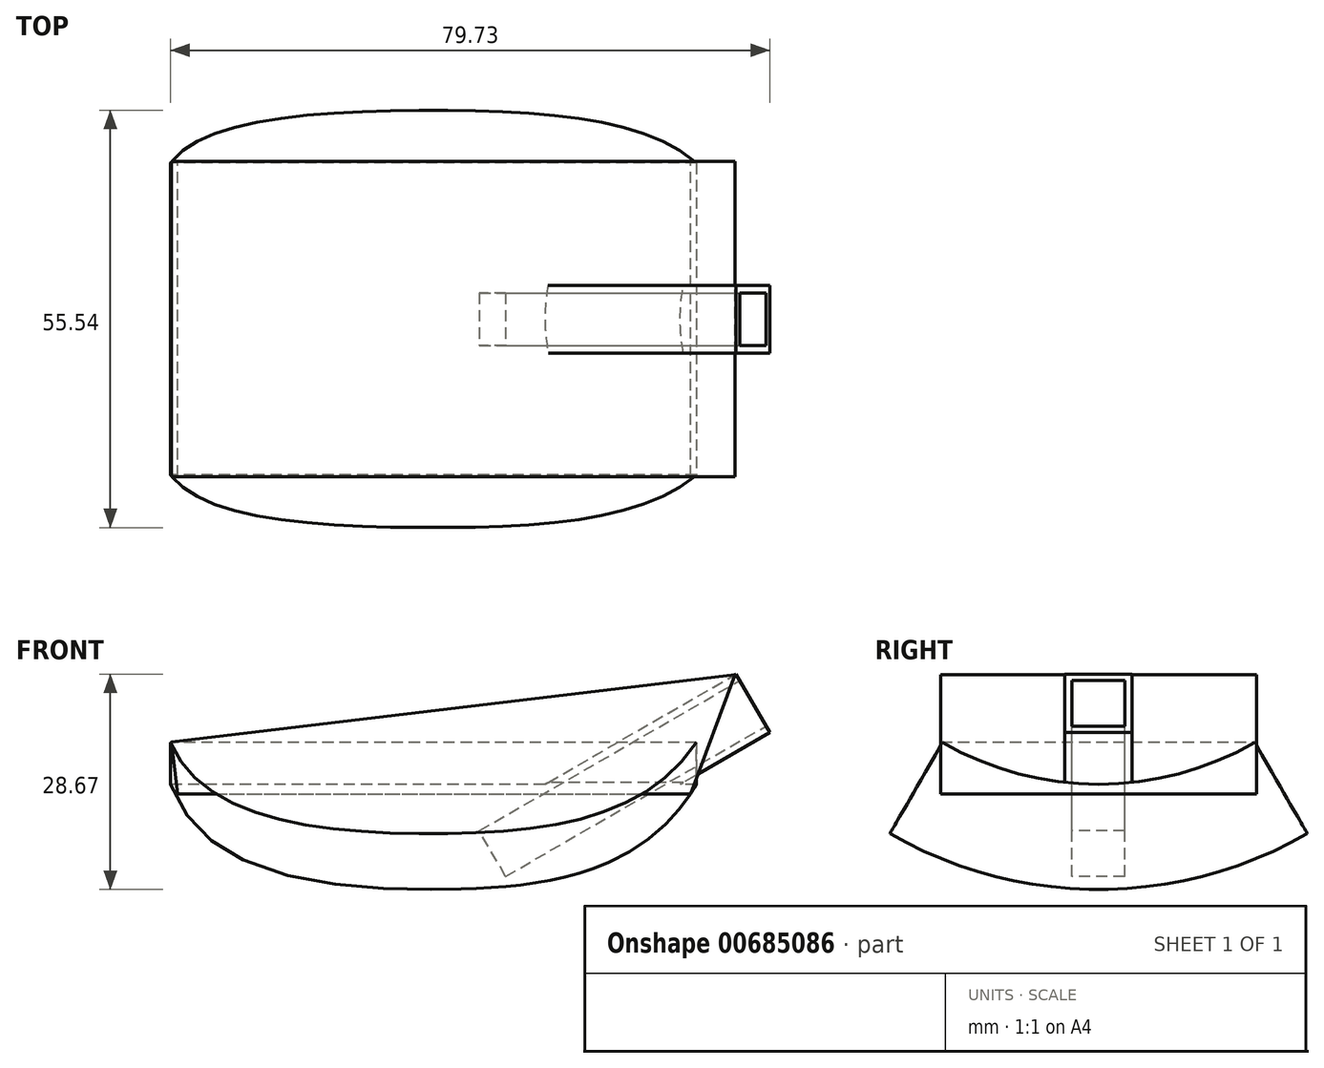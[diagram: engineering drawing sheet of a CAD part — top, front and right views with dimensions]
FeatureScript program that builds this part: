
annotation { "Feature Type Name" : "Feature", "Feature Type Description" : "" }
export const myFeature = defineFeature(function(context is Context, id is Id, definition is map)
    precondition{}
    {
        {
            var Q0;
            Q0=qCreatedBy(makeId("Front.planeOp"),FACE);
            var sketch = newSketch(context, id + "F0", { "sketchPlane" : qUnion([Q0])});
            skLineSegment(sketch, "E0", {"start": v(35, 14) * mm, "end": v(-35, 14) * mm});
            skFitSpline(sketch, "E1", {"points": [v(-35, 14) * mm, v(0, 0) * mm, v(35, 14) * mm], "startDerivative": vector(26.11, -73) * mm, "endDerivative": vector(42.26, 72.43) * mm});
            skLineSegment(sketch, "E2", {"start": v(-62.52, 55.54) * mm, "end": v(69.72, 55.54) * mm});
            skSolve(sketch);
        }
        {
            var Q0;
            Q0=makeQuery(id+"F0.imprint","IMPRINT",FACE,{"disambiguationData":[TD([[makeQuery(id+"F0.imprint","IMPRINT",EDGE,{"derivedFrom":sQuery(id+"F0.wireOp",EDGE,"E0")}),1.0]])]});
            var Q1;
            Q1=sQuery(id+"F0.wireOp",EDGE,"E2");
            revolve(context, id + "F1", {"entities" : qUnion([Q0]), "axis" : qUnion([Q1]), "revolveType" : RevolveType.SYMMETRIC, "angle" : 60 * degree});
        }
        {
            var Q0;
            Q0=qCreatedBy(makeId("Right.planeOp"),FACE);
            var sketch = newSketch(context, id + "F2", { "sketchPlane" : qUnion([Q0])});
            skLineSegment(sketch, "E3", {"start": v(-56.74, 68.36) * mm, "end": v(56.86, 68.36) * mm});
            skSolve(sketch);
        }
        {
            var Q0;
            Q0=qCreatedBy(makeId("Right.planeOp"),FACE);
            var Q1;
            Q1=sQuery(id+"F2.wireOp",EDGE,"E3");
            cPlane(context, id + "F3", {"entities" : qUnion([Q0, Q1]), "cplaneType" : CPlaneType.LINE_ANGLE, "offset" : 25 * mm, "angle" : 30 * degree, "oppositeDirection" : true, "width" : 150 * mm, "height" : 150 * mm});
        }
        {
            var Q0;
            Q0=qCreatedBy(id+"F3.planeOp",FACE);
            var sketch = newSketch(context, id + "F4", { "sketchPlane" : qUnion([Q0])});
            skPoint(sketch, "E4.middle", {"position": v(0.03, 0.21) * mm});
            skLineSegment(sketch, "E5.bottom", {"start": v(-4.47, 4.71) * mm, "end": v(4.53, 4.71) * mm});
            skLineSegment(sketch, "E5.top", {"start": v(-4.47, -4.29) * mm, "end": v(4.53, -4.29) * mm});
            skLineSegment(sketch, "E5.left", {"start": v(-4.47, 4.71) * mm, "end": v(-4.47, -4.29) * mm});
            skLineSegment(sketch, "E5.right", {"start": v(4.53, 4.71) * mm, "end": v(4.53, -4.29) * mm});
            skLineSegment(sketch, "E6.bottom", {"start": v(-3.47, -3.29) * mm, "end": v(3.53, -3.29) * mm});
            skLineSegment(sketch, "E6.top", {"start": v(-3.47, 3.71) * mm, "end": v(3.53, 3.71) * mm});
            skLineSegment(sketch, "E6.left", {"start": v(-3.47, -3.29) * mm, "end": v(-3.47, 3.71) * mm});
            skLineSegment(sketch, "E6.right", {"start": v(3.53, -3.29) * mm, "end": v(3.53, 3.71) * mm});
            skSolve(sketch);
        }
        {
            var Q0;
            Q0=makeQuery(id+"F4.imprint","IMPRINT",FACE,{"disambiguationData":[TD([[makeQuery(id+"F4.imprint","IMPRINT",EDGE,{"derivedFrom":sQuery(id+"F4.wireOp",EDGE,"E5.bottom")}),-1.0]])]});
            extrude(context, id + "F5", {"entities" : qUnion([Q0]), "operationType" : NewBodyOperationType.ADD, "depth" : 25 * mm, "offsetDistance" : 25 * mm});
        }
        {
            var Q0;
            Q0 = qSketchRegion(id + "F4", true);
            extrude(context, id + "F6", {"entities" : qUnion([Q0]), "operationType" : NewBodyOperationType.ADD, "oppositeDirection" : true, "depth" : 15 * mm, "offsetDistance" : 25 * mm});
        }
        {
            var Q0;
            Q0=makeQuery(id+"F4.imprint","IMPRINT",FACE,{"disambiguationData":[TD([[makeQuery(id+"F4.imprint","IMPRINT",EDGE,{"derivedFrom":sQuery(id+"F4.wireOp",EDGE,"E6.bottom")}),1.0]])]});
            extrude(context, id + "F7", {"entities" : qUnion([Q0]), "operationType" : NewBodyOperationType.REMOVE, "depth" : 25 * mm, "offsetDistance" : 25 * mm});
        }
        {
            var Q0;
            Q0=qCreatedBy(makeId("Front.planeOp"),FACE);
            var sketch = newSketch(context, id + "F8", { "sketchPlane" : qUnion([Q0])});
            skLineSegment(sketch, "E7", {"start": v(40.12, 28.58) * mm, "end": v(-34.9, 19.6) * mm});
            skLineSegment(sketch, "E8", {"start": v(-34.9, 19.6) * mm, "end": v(-34.08, 12.69) * mm});
            skLineSegment(sketch, "E9", {"start": v(-34.08, 12.69) * mm, "end": v(34.2, 12.69) * mm});
            skLineSegment(sketch, "E10", {"start": v(34.2, 12.69) * mm, "end": v(40.12, 28.58) * mm});
            skSolve(sketch);
        }
        {
            var Q0;
            Q0=makeQuery(id+"F8.imprint","IMPRINT",FACE,{"disambiguationData":[TD([[makeQuery(id+"F8.imprint","IMPRINT",EDGE,{"derivedFrom":sQuery(id+"F8.wireOp",EDGE,"E7")}),1.0]])]});
            extrude(context, id + "F9", {"entities" : qUnion([Q0]), "endBound" : BoundingType.SYMMETRIC, "depth" : 42 * mm, "offsetDistance" : 25 * mm});
        }
    });
